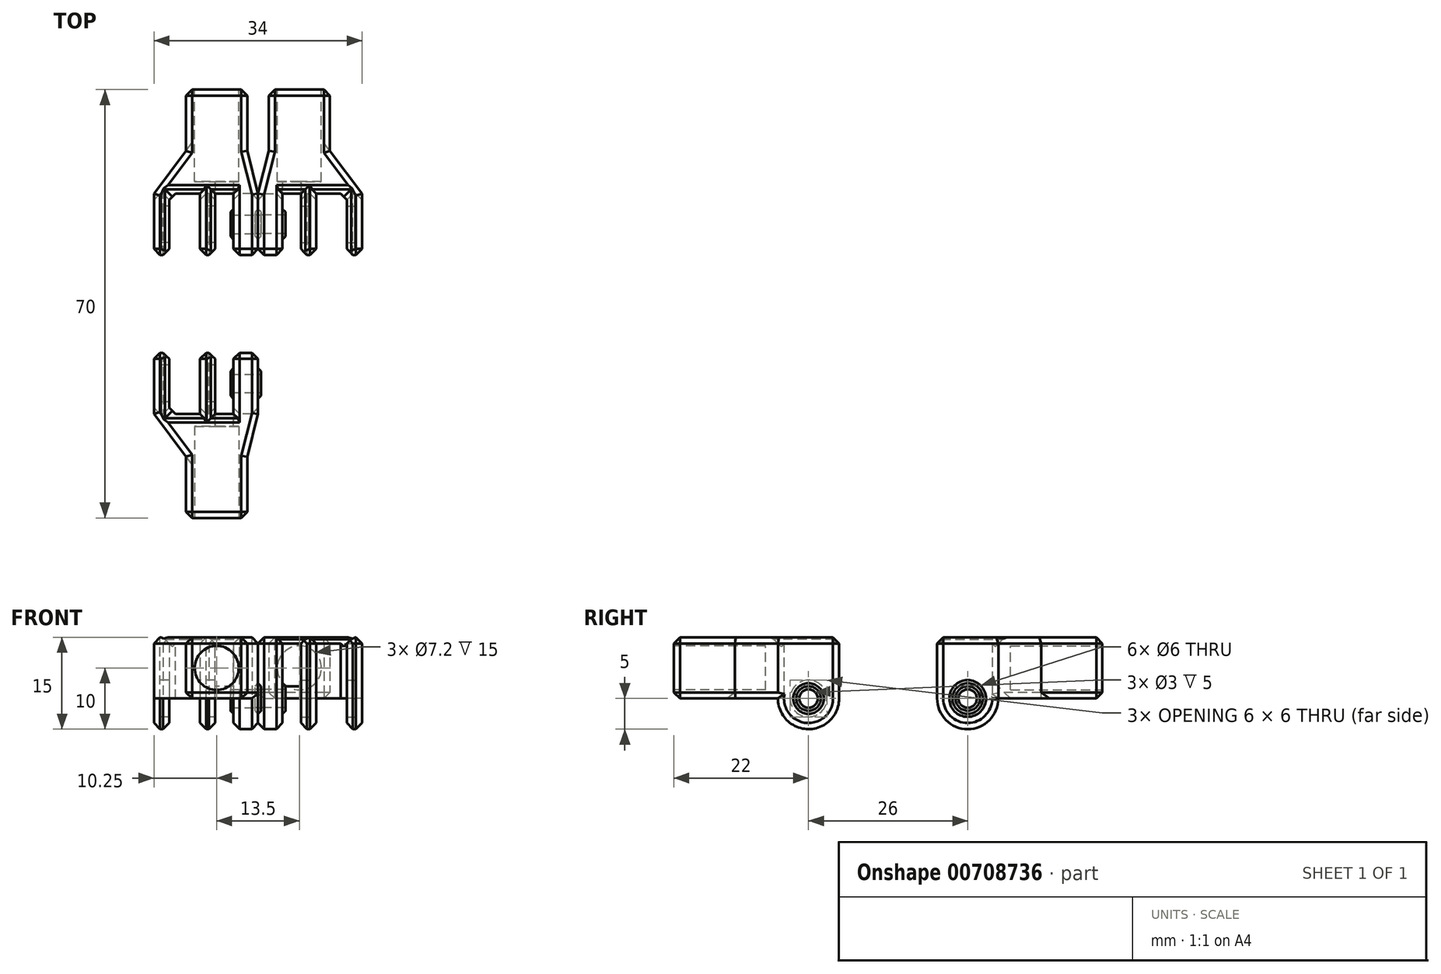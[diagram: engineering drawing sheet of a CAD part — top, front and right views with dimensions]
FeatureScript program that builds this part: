
annotation { "Feature Type Name" : "Feature", "Feature Type Description" : "" }
export const myFeature = defineFeature(function(context is Context, id is Id, definition is map)
    precondition{}
    {
        {
            var Q0;
            Q0=qCreatedBy(makeId("Top.planeOp"),FACE);
            var sketch = newSketch(context, id + "F0", { "sketchPlane" : qUnion([Q0])});
            skLineSegment(sketch, "E0", {"start": v(-5, 0) * mm, "end": v(-5, -10) * mm});
            skLineSegment(sketch, "E1", {"start": v(-5, -10) * mm, "end": v(5, -10) * mm});
            skLineSegment(sketch, "E2", {"start": v(5, -10) * mm, "end": v(5, 0) * mm});
            skLineSegment(sketch, "E3", {"start": v(5, 0) * mm, "end": v(6.75, 7) * mm});
            skLineSegment(sketch, "E4", {"start": v(6.75, 7) * mm, "end": v(-10.25, 7) * mm});
            skLineSegment(sketch, "E5", {"start": v(-10.25, 7) * mm, "end": v(-5, 0) * mm});
            skSolve(sketch);
        }
        {
            var Q0;
            Q0 = qSketchRegion(id + "F0", true);
            extrude(context, id + "F1", {"entities" : qUnion([Q0]), "depth" : 10 * mm, "offsetDistance" : 25 * mm});
        }
        {
            var Q0;
            Q0=makeQuery(id+"F1.opExtrude","SWEPT_FACE",FACE,{"disambiguationData":[OSD([sQuery(id+"F0.wireOp",EDGE,"E1")])]});
            var sketch = newSketch(context, id + "F2", { "sketchPlane" : qUnion([Q0])});
            skCircle(sketch, "E6", {"center": v(0, 5) * mm, "radius": 3.6 * mm});
            skSolve(sketch);
        }
        {
            var Q0;
            Q0 = qSketchRegion(id + "F2", true);
            extrude(context, id + "F3", {"entities" : qUnion([Q0]), "operationType" : NewBodyOperationType.REMOVE, "oppositeDirection" : true, "depth" : 15 * mm, "offsetDistance" : 25 * mm});
        }
        {
            var Q0;
            Q0=qCreatedBy(makeId("Right.planeOp"),FACE);
            cPlane(context, id + "F4", {"entities" : qUnion([Q0]), "cplaneType" : CPlaneType.OFFSET, "offset" : 10.25 * mm, "oppositeDirection" : true, "width" : 150 * mm, "height" : 150 * mm});
        }
        {
            var Q0;
            Q0=qCreatedBy(id+"F4.planeOp",FACE);
            var sketch = newSketch(context, id + "F5", { "sketchPlane" : qUnion([Q0])});
            skLineSegment(sketch, "E7", {"start": v(7, 10) * mm, "end": v(17, 10) * mm});
            skLineSegment(sketch, "E8", {"start": v(17, 10) * mm, "end": v(17, -5) * mm});
            skLineSegment(sketch, "E9", {"start": v(17, -5) * mm, "end": v(7, -5) * mm});
            skLineSegment(sketch, "E10", {"start": v(7, -5) * mm, "end": v(7, 0) * mm});
            skLineSegment(sketch, "E11", {"start": v(7, 0) * mm, "end": v(7, 10) * mm});
            skCircle(sketch, "E12", {"center": v(12, 0) * mm, "radius": 3 * mm});
            skSolve(sketch);
        }
        {
            var Q0;
            Q0=makeQuery(id+"F5.imprint","IMPRINT",FACE,{"disambiguationData":[TD([[makeQuery(id+"F5.imprint","IMPRINT",EDGE,{"derivedFrom":sQuery(id+"F5.wireOp",EDGE,"E7")}),-1.0]])]});
            extrude(context, id + "F6", {"entities" : qUnion([Q0]), "operationType" : NewBodyOperationType.ADD, "depth" : 10 * mm, "offsetDistance" : 25 * mm});
        }
        {
            var Q0;
            Q0=makeQuery(id+"F6.opExtrude","SWEPT_FACE",FACE,{"disambiguationData":[OSD([sQuery(id+"F5.wireOp",EDGE,"E9")])]});
            var sketch = newSketch(context, id + "F7", { "sketchPlane" : qUnion([Q0])});
            skLineSegment(sketch, "E13.bottom", {"start": v(-7.75, -7) * mm, "end": v(-2.75, -7) * mm});
            skLineSegment(sketch, "E13.top", {"start": v(-7.75, -17) * mm, "end": v(-2.75, -17) * mm});
            skLineSegment(sketch, "E13.left", {"start": v(-7.75, -7) * mm, "end": v(-7.75, -17) * mm});
            skLineSegment(sketch, "E13.right", {"start": v(-2.75, -7) * mm, "end": v(-2.75, -17) * mm});
            skSolve(sketch);
        }
        {
            var Q0;
            Q0 = qSketchRegion(id + "F7", true);
            extrude(context, id + "F8", {"entities" : qUnion([Q0]), "operationType" : NewBodyOperationType.REMOVE, "oppositeDirection" : true, "depth" : 25 * mm, "offsetDistance" : 25 * mm});
        }
        {
            var Q0;
            Q0=qCreatedBy(makeId("Right.planeOp"),FACE);
            cPlane(context, id + "F9", {"entities" : qUnion([Q0]), "cplaneType" : CPlaneType.OFFSET, "offset" : 6.75 * mm, "width" : 150 * mm, "height" : 150 * mm});
        }
        {
            var Q0;
            Q0=qCreatedBy(id+"F9.planeOp",FACE);
            var sketch = newSketch(context, id + "F10", { "sketchPlane" : qUnion([Q0])});
            skLineSegment(sketch, "E14", {"start": v(7, 10) * mm, "end": v(17, 10) * mm});
            skLineSegment(sketch, "E15", {"start": v(17, 10) * mm, "end": v(17, -5) * mm});
            skLineSegment(sketch, "E16", {"start": v(17, -5) * mm, "end": v(7, -5) * mm});
            skLineSegment(sketch, "E17", {"start": v(7, -5) * mm, "end": v(7, 10) * mm});
            skCircle(sketch, "E18", {"center": v(12, 0) * mm, "radius": 1.5 * mm});
            skSolve(sketch);
        }
        {
            var Q0;
            Q0 = qSketchRegion(id + "F10", true);
            extrude(context, id + "F11", {"entities" : qUnion([Q0]), "operationType" : NewBodyOperationType.ADD, "oppositeDirection" : true, "depth" : 4 * mm, "offsetDistance" : 25 * mm});
        }
        {
            var Q0;
            Q0=makeQuery(id+"F11.opExtrude","CAP_FACE",FACE,{"disambiguationData":[OSD([sQuery(id+"F10.wireOp",EDGE,"E14"),sQuery(id+"F10.wireOp",EDGE,"E15"),sQuery(id+"F10.wireOp",EDGE,"E16"),sQuery(id+"F10.wireOp",EDGE,"E17"),sQuery(id+"F10.wireOp",EDGE,"E18")])],"isStart":true});
            var sketch = newSketch(context, id + "F12", { "sketchPlane" : qUnion([Q0])});
            skCircle(sketch, "E19", {"center": v(12, 0) * mm, "radius": 2.5 * mm});
            skCircle(sketch, "E20", {"center": v(12, 0) * mm, "radius": 1.5 * mm});
            skSolve(sketch);
        }
        {
            var Q0;
            Q0 = qSketchRegion(id + "F12", true);
            extrude(context, id + "F13", {"entities" : qUnion([Q0]), "operationType" : NewBodyOperationType.ADD, "depth" : 0.5 * mm, "offsetDistance" : 25 * mm});
        }
        {
            var Q0;
            Q0=makeQuery(id+"F13.opExtrude","CAP_EDGE",EDGE,{"disambiguationData":[OSD([sQuery(id+"F12.wireOp",EDGE,"E19")])],"isStart":true});
            var Q1;
            Q1=makeQuery(id+"F13.opExtrude","CAP_EDGE",EDGE,{"disambiguationData":[OSD([sQuery(id+"F12.wireOp",EDGE,"E19")])],"isStart":false});
            chamfer(context, id + "F14", {"entities" : qUnion([Q0, Q1]), "width" : 0.5 * mm, "tangentPropagation" : true});
        }
        {
            var Q0;
            Q0=makeQuery(id+"F11.opExtrude","CAP_FACE",FACE,{"disambiguationData":[OSD([sQuery(id+"F10.wireOp",EDGE,"E14"),sQuery(id+"F10.wireOp",EDGE,"E15"),sQuery(id+"F10.wireOp",EDGE,"E16"),sQuery(id+"F10.wireOp",EDGE,"E17"),sQuery(id+"F10.wireOp",EDGE,"E18")])],"isStart":false});
            var sketch = newSketch(context, id + "F15", { "sketchPlane" : qUnion([Q0])});
            skCircle(sketch, "E21", {"center": v(-12, 0) * mm, "radius": 2.5 * mm});
            skCircle(sketch, "E22", {"center": v(-12, 0) * mm, "radius": 1.5 * mm});
            skSolve(sketch);
        }
        {
            var Q0;
            Q0 = qSketchRegion(id + "F15", true);
            extrude(context, id + "F16", {"entities" : qUnion([Q0]), "operationType" : NewBodyOperationType.ADD, "depth" : 0.5 * mm, "offsetDistance" : 25 * mm});
        }
        {
            var Q0;
            Q0=makeQuery(id+"F13.opExtrude","CAP_EDGE",EDGE,{"disambiguationData":[OSD([sQuery(id+"F12.wireOp",EDGE,"E19")])],"isStart":false});
            var Q1;
            Q1=makeQuery(id+"F16.opExtrude","CAP_EDGE",EDGE,{"disambiguationData":[OSD([sQuery(id+"F15.wireOp",EDGE,"E21")])],"isStart":false});
            chamfer(context, id + "F17", {"entities" : qUnion([Q0, Q1]), "width" : 0.5 * mm, "tangentPropagation" : true});
        }
        {
            var Q0;
            Q0=makeQuery(id+"F11.opExtrude","SWEPT_EDGE",EDGE,{"disambiguationData":[OSD([sQuery(id+"F10.wireOp",EDGE,"E16"),sQuery(id+"F10.wireOp",EDGE,"E17")])]});
            var Q1;
            Q1=makeQuery(id+"F11.opExtrude","SWEPT_EDGE",EDGE,{"disambiguationData":[OSD([sQuery(id+"F10.wireOp",EDGE,"E15"),sQuery(id+"F10.wireOp",EDGE,"E16")])]});
            var Q2;
            {var subQ1=sQuery(id+"F5.wireOp",EDGE,"E10");var subQ2=sQuery(id+"F5.wireOp",EDGE,"E9");Q2=makeQuery(id+"F8.boolean.opBoolean","SPLIT",EDGE,{"disambiguationData":[TD([makeQuery(id+"F8.opExtrude","SWEPT_FACE",FACE,{"disambiguationData":[OSD([sQuery(id+"F7.wireOp",EDGE,"E13.right")])]})])],"derivedFrom":makeQuery(id+"F6.opExtrude","SWEPT_EDGE",EDGE,{"disambiguationData":[OSD([subQ2,subQ1])]})});}
            var Q3;
            {var subQ0=sQuery(id+"F5.wireOp",EDGE,"E9");var subQ1=sQuery(id+"F5.wireOp",EDGE,"E8");Q3=makeQuery(id+"F8.boolean.opBoolean","SPLIT",EDGE,{"disambiguationData":[TD([makeQuery(id+"F8.opExtrude","SWEPT_FACE",FACE,{"disambiguationData":[OSD([sQuery(id+"F7.wireOp",EDGE,"E13.right")])]})])],"derivedFrom":makeQuery(id+"F6.opExtrude","SWEPT_EDGE",EDGE,{"disambiguationData":[OSD([subQ1,subQ0])]})});}
            var Q4;
            {var subQ1=sQuery(id+"F5.wireOp",EDGE,"E10");var subQ2=sQuery(id+"F5.wireOp",EDGE,"E9");Q4=makeQuery(id+"F8.boolean.opBoolean","SPLIT",EDGE,{"disambiguationData":[TD([makeQuery(id+"F8.opExtrude","SWEPT_FACE",FACE,{"disambiguationData":[OSD([sQuery(id+"F7.wireOp",EDGE,"E13.left")])]})])],"derivedFrom":makeQuery(id+"F6.opExtrude","SWEPT_EDGE",EDGE,{"disambiguationData":[OSD([subQ2,subQ1])]})});}
            var Q5;
            {var subQ0=sQuery(id+"F5.wireOp",EDGE,"E9");var subQ1=sQuery(id+"F5.wireOp",EDGE,"E8");Q5=makeQuery(id+"F8.boolean.opBoolean","SPLIT",EDGE,{"disambiguationData":[TD([makeQuery(id+"F8.opExtrude","SWEPT_FACE",FACE,{"disambiguationData":[OSD([sQuery(id+"F7.wireOp",EDGE,"E13.left")])]})])],"derivedFrom":makeQuery(id+"F6.opExtrude","SWEPT_EDGE",EDGE,{"disambiguationData":[OSD([subQ1,subQ0])]})});}
            fillet(context, id + "F18", {"entities" : qUnion([Q0, Q1, Q2, Q3, Q4, Q5]), "radius" : 5 * mm, "tangentPropagation" : true, "allowEdgeOverflow" : false});
        }
        {
            var Q0;
            {var subQ0=sQuery(id+"F0.wireOp",EDGE,"E4");var subQ1=makeQuery(id+"F1.opExtrude","CAP_FACE",FACE,{"disambiguationData":[OSD([sQuery(id+"F0.wireOp",EDGE,"E0"),sQuery(id+"F0.wireOp",EDGE,"E1"),sQuery(id+"F0.wireOp",EDGE,"E2"),sQuery(id+"F0.wireOp",EDGE,"E3"),subQ0,sQuery(id+"F0.wireOp",EDGE,"E5")])],"isStart":true});Q0=makeQuery(id+"F8.boolean.opBoolean","SPLIT",EDGE,{"disambiguationData":[topologyDisambiguationEdgeConnected([subQ1,makeQuery(id+"F8.opExtrude","SWEPT_FACE",FACE,{"disambiguationData":[OSD([sQuery(id+"F7.wireOp",EDGE,"E13.bottom")])]})])],"derivedFrom":makeQuery(id+"F6.boolean.opBoolean","SPLIT",EDGE,{"disambiguationData":[topologyDisambiguationEdgeConnected([makeQuery(id+"F6.opExtrude","SWEPT_FACE",FACE,{"disambiguationData":[OSD([sQuery(id+"F5.wireOp",EDGE,"E10"),sQuery(id+"F5.wireOp",EDGE,"E11")])]})])],"derivedFrom":makeQuery(id+"F1.opExtrude","CAP_EDGE",EDGE,{"disambiguationData":[OSD([subQ0])],"isStart":true})})});}
            var Q1;
            {var subQ0=sQuery(id+"F0.wireOp",EDGE,"E4");var subQ2=makeQuery(id+"F1.opExtrude","SWEPT_FACE",FACE,{"disambiguationData":[OSD([subQ0])]});Q1=makeQuery(id+"F11.boolean.opBoolean","SPLIT",EDGE,{"disambiguationData":[topologyDisambiguationEdgeConnected([subQ2])],"derivedFrom":makeQuery(id+"F6.boolean.opBoolean","SPLIT",EDGE,{"disambiguationData":[topologyDisambiguationEdgeConnected([subQ2])],"derivedFrom":makeQuery(id+"F1.opExtrude","CAP_EDGE",EDGE,{"disambiguationData":[OSD([subQ0])],"isStart":true})})});}
            chamfer(context, id + "F19", {"entities" : qUnion([Q0, Q1]), "width" : 2 * mm, "tangentPropagation" : true});
        }
        {
            var Q0;
            Q0=makeQuery(id+"F8.boolean.opBoolean","INTERSECT",EDGE,{"derivedFrom":[makeQuery(id+"F6.boolean.opBoolean","MERGE",FACE,{"derivedFrom":[makeQuery(id+"F1.opExtrude","CAP_FACE",FACE,{"disambiguationData":[OSD([sQuery(id+"F0.wireOp",EDGE,"E0"),sQuery(id+"F0.wireOp",EDGE,"E1"),sQuery(id+"F0.wireOp",EDGE,"E2"),sQuery(id+"F0.wireOp",EDGE,"E3"),sQuery(id+"F0.wireOp",EDGE,"E4"),sQuery(id+"F0.wireOp",EDGE,"E5")])],"isStart":false}),makeQuery(id+"F6.opExtrude","SWEPT_FACE",FACE,{"disambiguationData":[OSD([sQuery(id+"F5.wireOp",EDGE,"E7")])]})]}),makeQuery(id+"F8.opExtrude","SWEPT_FACE",FACE,{"disambiguationData":[OSD([sQuery(id+"F7.wireOp",EDGE,"E13.left")])]})]});
            var Q1;
            Q1=makeQuery(id+"F8.boolean.opBoolean","INTERSECT",EDGE,{"derivedFrom":[makeQuery(id+"F6.boolean.opBoolean","MERGE",FACE,{"derivedFrom":[makeQuery(id+"F1.opExtrude","CAP_FACE",FACE,{"disambiguationData":[OSD([sQuery(id+"F0.wireOp",EDGE,"E0"),sQuery(id+"F0.wireOp",EDGE,"E1"),sQuery(id+"F0.wireOp",EDGE,"E2"),sQuery(id+"F0.wireOp",EDGE,"E3"),sQuery(id+"F0.wireOp",EDGE,"E4"),sQuery(id+"F0.wireOp",EDGE,"E5")])],"isStart":false}),makeQuery(id+"F6.opExtrude","SWEPT_FACE",FACE,{"disambiguationData":[OSD([sQuery(id+"F5.wireOp",EDGE,"E7")])]})]}),makeQuery(id+"F8.opExtrude","SWEPT_FACE",FACE,{"disambiguationData":[OSD([sQuery(id+"F7.wireOp",EDGE,"E13.bottom")])]})]});
            var Q2;
            Q2=makeQuery(id+"F1.opExtrude","CAP_EDGE",EDGE,{"disambiguationData":[OSD([sQuery(id+"F0.wireOp",EDGE,"E4")])],"isStart":false});
            var Q3;
            Q3=makeQuery(id+"F6.opExtrude","CAP_EDGE",EDGE,{"disambiguationData":[OSD([sQuery(id+"F5.wireOp",EDGE,"E7")])],"isStart":false});
            chamfer(context, id + "F20", {"entities" : qUnion([Q0, Q1, Q2, Q3]), "width" : 1 * mm, "tangentPropagation" : true});
        }
        {
            var Q0;
            Q0=makeQuery(id+"F1.opExtrude","CAP_EDGE",EDGE,{"disambiguationData":[OSD([sQuery(id+"F0.wireOp",EDGE,"E3")])],"isStart":true});
            var Q1;
            {var subQ0=sQuery(id+"F5.wireOp",EDGE,"E11");var subQ1=sQuery(id+"F5.wireOp",EDGE,"E10");Q1=makeQuery(id+"F6.boolean.opBoolean","SPLIT",EDGE,{"disambiguationData":[topologyDisambiguationEdgeConnected([makeQuery(id+"F6.opExtrude","SWEPT_FACE",FACE,{"disambiguationData":[OSD([subQ1,subQ0])]})])],"derivedFrom":makeQuery(id+"F6.opExtrude","CAP_EDGE",EDGE,{"disambiguationData":[OSD([subQ1,subQ0])],"isStart":false})});}
            var Q2;
            {var subQ0=sQuery(id+"F5.wireOp",EDGE,"E10");var subQ1=sQuery(id+"F7.wireOp",EDGE,"E13.left");Q2=makeQuery(id+"F8.boolean.opBoolean","COPY",EDGE,{"disambiguationData":[topologyDisambiguationEdgeConnected([makeQuery(id+"F6.opExtrude","SWEPT_FACE",FACE,{"disambiguationData":[OSD([subQ0,sQuery(id+"F5.wireOp",EDGE,"E11")])]})])],"derivedFrom":makeQuery(id+"F8.opExtrude","SWEPT_EDGE",EDGE,{"disambiguationData":[OSD([sQuery(id+"F5.wireOp",EDGE,"E9"),subQ0,sQuery(id+"F7.wireOp",EDGE,"E13.bottom"),subQ1])]})});}
            chamfer(context, id + "F21", {"entities" : qUnion([Q0, Q1, Q2]), "width" : 1 * mm, "tangentPropagation" : true});
        }
        {
            var Q0;
            Q0=makeQuery(id+"F1.opExtrude","CAP_EDGE",EDGE,{"disambiguationData":[OSD([sQuery(id+"F0.wireOp",EDGE,"E0")])],"isStart":true});
            var Q1;
            {var subQ0=sQuery(id+"F5.wireOp",EDGE,"E9");var subQ1=sQuery(id+"F5.wireOp",EDGE,"E8");var subQ2=makeQuery(id+"F6.opExtrude","CAP_FACE",FACE,{"disambiguationData":[OSD([sQuery(id+"F5.wireOp",EDGE,"E7"),subQ1,subQ0,sQuery(id+"F5.wireOp",EDGE,"E10"),sQuery(id+"F5.wireOp",EDGE,"E11"),sQuery(id+"F5.wireOp",EDGE,"E12")])],"isStart":true});Q1=makeQuery(id+"F18.opFillet","BLEND_EDGE",EDGE,{"blendedFrom":[makeQuery(id+"F8.boolean.opBoolean","SPLIT",EDGE,{"disambiguationData":[TD([makeQuery(id+"F8.opExtrude","SWEPT_FACE",FACE,{"disambiguationData":[OSD([sQuery(id+"F7.wireOp",EDGE,"E13.left")])]})])],"derivedFrom":makeQuery(id+"F6.opExtrude","SWEPT_EDGE",EDGE,{"disambiguationData":[OSD([subQ1,subQ0])]})}),subQ2],"blendedInto":[subQ2]});}
            var Q2;
            {var subQ0=makeQuery(id+"F8.opExtrude","SWEPT_FACE",FACE,{"disambiguationData":[OSD([sQuery(id+"F7.wireOp",EDGE,"E13.left")])]});var subQ1=sQuery(id+"F5.wireOp",EDGE,"E9");var subQ2=sQuery(id+"F5.wireOp",EDGE,"E8");Q2=makeQuery(id+"F18.opFillet","BLEND_EDGE",EDGE,{"blendedFrom":[makeQuery(id+"F8.boolean.opBoolean","SPLIT",EDGE,{"disambiguationData":[TD([subQ0])],"derivedFrom":makeQuery(id+"F6.opExtrude","SWEPT_EDGE",EDGE,{"disambiguationData":[OSD([subQ2,subQ1])]})}),makeQuery(id+"F8.boolean.opBoolean","COPY",FACE,{"derivedFrom":subQ0})],"blendedInto":[makeQuery(id+"F8.boolean.opBoolean","COPY",FACE,{"derivedFrom":subQ0})]});}
            var Q3;
            {var subQ0=makeQuery(id+"F8.opExtrude","SWEPT_FACE",FACE,{"disambiguationData":[OSD([sQuery(id+"F7.wireOp",EDGE,"E13.right")])]});var subQ1=sQuery(id+"F5.wireOp",EDGE,"E9");var subQ2=sQuery(id+"F5.wireOp",EDGE,"E8");Q3=makeQuery(id+"F18.opFillet","BLEND_EDGE",EDGE,{"blendedFrom":[makeQuery(id+"F8.boolean.opBoolean","SPLIT",EDGE,{"disambiguationData":[TD([subQ0])],"derivedFrom":makeQuery(id+"F6.opExtrude","SWEPT_EDGE",EDGE,{"disambiguationData":[OSD([subQ2,subQ1])]})}),makeQuery(id+"F8.boolean.opBoolean","COPY",FACE,{"derivedFrom":subQ0})],"blendedInto":[makeQuery(id+"F8.boolean.opBoolean","COPY",FACE,{"derivedFrom":subQ0})]});}
            var Q4;
            {var subQ0=sQuery(id+"F5.wireOp",EDGE,"E9");var subQ1=sQuery(id+"F5.wireOp",EDGE,"E8");var subQ2=makeQuery(id+"F6.opExtrude","CAP_FACE",FACE,{"disambiguationData":[OSD([sQuery(id+"F5.wireOp",EDGE,"E7"),subQ1,subQ0,sQuery(id+"F5.wireOp",EDGE,"E10"),sQuery(id+"F5.wireOp",EDGE,"E11"),sQuery(id+"F5.wireOp",EDGE,"E12")])],"isStart":false});Q4=makeQuery(id+"F18.opFillet","BLEND_EDGE",EDGE,{"blendedFrom":[makeQuery(id+"F8.boolean.opBoolean","SPLIT",EDGE,{"disambiguationData":[TD([makeQuery(id+"F8.opExtrude","SWEPT_FACE",FACE,{"disambiguationData":[OSD([sQuery(id+"F7.wireOp",EDGE,"E13.right")])]})])],"derivedFrom":makeQuery(id+"F6.opExtrude","SWEPT_EDGE",EDGE,{"disambiguationData":[OSD([subQ1,subQ0])]})}),subQ2],"blendedInto":[subQ2]});}
            var Q5;
            {var subQ0=sQuery(id+"F10.wireOp",EDGE,"E16");var subQ1=sQuery(id+"F10.wireOp",EDGE,"E15");Q5=makeQuery(id+"F18.opFillet","BLEND_EDGE",EDGE,{"blendedFrom":[makeQuery(id+"F11.opExtrude","SWEPT_EDGE",EDGE,{"disambiguationData":[OSD([subQ1,subQ0])]}),makeQuery(id+"F11.opExtrude","CAP_FACE",FACE,{"disambiguationData":[OSD([sQuery(id+"F10.wireOp",EDGE,"E14"),subQ1,subQ0,sQuery(id+"F10.wireOp",EDGE,"E17"),sQuery(id+"F10.wireOp",EDGE,"E18")])],"isStart":false})],"blendedInto":[makeQuery(id+"F11.opExtrude","CAP_FACE",FACE,{"disambiguationData":[OSD([sQuery(id+"F10.wireOp",EDGE,"E14"),subQ1,subQ0,sQuery(id+"F10.wireOp",EDGE,"E17"),sQuery(id+"F10.wireOp",EDGE,"E18")])],"isStart":false})]});}
            var Q6;
            {var subQ0=sQuery(id+"F10.wireOp",EDGE,"E16");var subQ1=sQuery(id+"F10.wireOp",EDGE,"E15");Q6=makeQuery(id+"F18.opFillet","BLEND_EDGE",EDGE,{"blendedFrom":[makeQuery(id+"F11.opExtrude","SWEPT_EDGE",EDGE,{"disambiguationData":[OSD([subQ1,subQ0])]}),makeQuery(id+"F11.opExtrude","CAP_FACE",FACE,{"disambiguationData":[OSD([sQuery(id+"F10.wireOp",EDGE,"E14"),subQ1,subQ0,sQuery(id+"F10.wireOp",EDGE,"E17"),sQuery(id+"F10.wireOp",EDGE,"E18")])],"isStart":true})],"blendedInto":[makeQuery(id+"F11.opExtrude","CAP_FACE",FACE,{"disambiguationData":[OSD([sQuery(id+"F10.wireOp",EDGE,"E14"),subQ1,subQ0,sQuery(id+"F10.wireOp",EDGE,"E17"),sQuery(id+"F10.wireOp",EDGE,"E18")])],"isStart":true})]});}
            var Q7;
            Q7=makeQuery(id+"F1.opExtrude","CAP_EDGE",EDGE,{"disambiguationData":[OSD([sQuery(id+"F0.wireOp",EDGE,"E2")])],"isStart":true});
            var Q8;
            Q8=makeQuery(id+"F1.opExtrude","CAP_EDGE",EDGE,{"disambiguationData":[OSD([sQuery(id+"F0.wireOp",EDGE,"E1")])],"isStart":true});
            var Q9;
            Q9=makeQuery(id+"F1.opExtrude","SWEPT_EDGE",EDGE,{"disambiguationData":[OSD([sQuery(id+"F0.wireOp",EDGE,"E0"),sQuery(id+"F0.wireOp",EDGE,"E1")])]});
            var Q10;
            Q10=makeQuery(id+"F1.opExtrude","CAP_EDGE",EDGE,{"disambiguationData":[OSD([sQuery(id+"F0.wireOp",EDGE,"E0")])],"isStart":false});
            var Q11;
            Q11=makeQuery(id+"F1.opExtrude","CAP_EDGE",EDGE,{"disambiguationData":[OSD([sQuery(id+"F0.wireOp",EDGE,"E5")])],"isStart":false});
            var Q12;
            Q12=makeQuery(id+"F6.opExtrude","CAP_EDGE",EDGE,{"disambiguationData":[OSD([sQuery(id+"F5.wireOp",EDGE,"E7")])],"isStart":true});
            var Q13;
            Q13=makeQuery(id+"F11.boolean.opBoolean","MERGE",FACE,{"derivedFrom":[makeQuery(id+"F6.boolean.opBoolean","MERGE",FACE,{"derivedFrom":[makeQuery(id+"F1.opExtrude","CAP_FACE",FACE,{"disambiguationData":[OSD([sQuery(id+"F0.wireOp",EDGE,"E0"),sQuery(id+"F0.wireOp",EDGE,"E1"),sQuery(id+"F0.wireOp",EDGE,"E2"),sQuery(id+"F0.wireOp",EDGE,"E3"),sQuery(id+"F0.wireOp",EDGE,"E4"),sQuery(id+"F0.wireOp",EDGE,"E5")])],"isStart":false}),makeQuery(id+"F6.opExtrude","SWEPT_FACE",FACE,{"disambiguationData":[OSD([sQuery(id+"F5.wireOp",EDGE,"E7")])]})]}),makeQuery(id+"F11.opExtrude","SWEPT_FACE",FACE,{"disambiguationData":[OSD([sQuery(id+"F10.wireOp",EDGE,"E14")])]})]});
            var Q14;
            Q14=makeQuery(id+"F1.opExtrude","SWEPT_EDGE",EDGE,{"disambiguationData":[OSD([sQuery(id+"F0.wireOp",EDGE,"E1"),sQuery(id+"F0.wireOp",EDGE,"E2")])]});
            chamfer(context, id + "F22", {"entities" : qUnion([Q0, Q1, Q2, Q3, Q4, Q5, Q6, Q7, Q8, Q9, Q10, Q11, Q12, Q13, Q14]), "width" : 1 * mm, "tangentPropagation" : true});
        }
        {
            var Q0;
            Q0=qCreatedBy(makeId("Front.planeOp"),FACE);
            cPlane(context, id + "F23", {"entities" : qUnion([Q0]), "cplaneType" : CPlaneType.OFFSET, "offset" : 25 * mm, "oppositeDirection" : true, "width" : 150 * mm, "height" : 150 * mm});
        }
        {
            var Q0;
            Q0=makeQuery(id+"F1.opExtrude","SWEPT_BODY",BODY,{"disambiguationData":[OSD([sQuery(id+"F0.wireOp",EDGE,"E0"),sQuery(id+"F0.wireOp",EDGE,"E1"),sQuery(id+"F0.wireOp",EDGE,"E2"),sQuery(id+"F0.wireOp",EDGE,"E3"),sQuery(id+"F0.wireOp",EDGE,"E4"),sQuery(id+"F0.wireOp",EDGE,"E5")])]});
            var Q1;
            Q1=qCreatedBy(id+"F23.planeOp",FACE);
            mirror(context, id + "F24", {"entities" : qUnion([Q0]), "mirrorPlane" : qUnion([Q1])});
        }
        {
            var Q0;
            Q0=makeQuery(id+"F24.opPattern","COPY",BODY,{"derivedFrom":makeQuery(id+"F1.opExtrude","SWEPT_BODY",BODY,{"disambiguationData":[OSD([sQuery(id+"F0.wireOp",EDGE,"E0"),sQuery(id+"F0.wireOp",EDGE,"E1"),sQuery(id+"F0.wireOp",EDGE,"E2"),sQuery(id+"F0.wireOp",EDGE,"E3"),sQuery(id+"F0.wireOp",EDGE,"E4"),sQuery(id+"F0.wireOp",EDGE,"E5")])]}),"instanceName":"1"});
            var Q1;
            Q1=qCreatedBy(id+"F9.planeOp",FACE);
            mirror(context, id + "F25", {"entities" : qUnion([Q0]), "mirrorPlane" : qUnion([Q1])});
        }
    });
